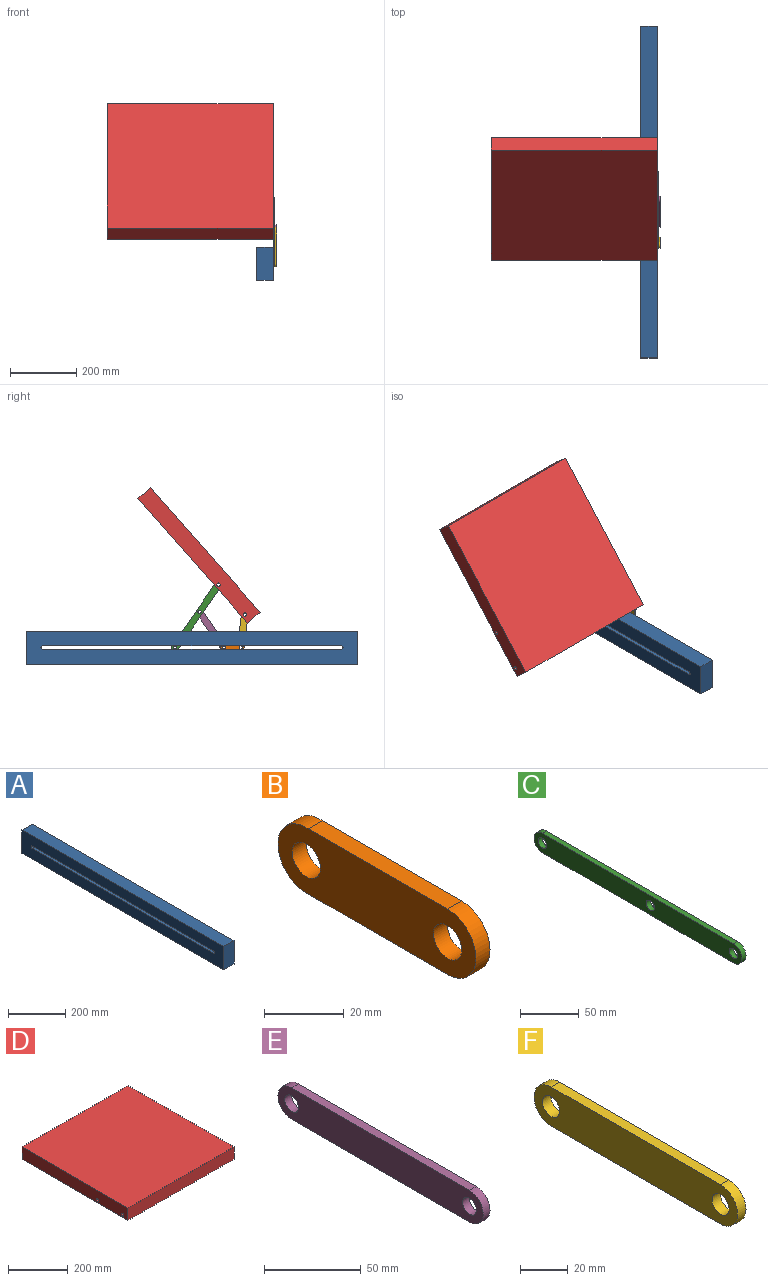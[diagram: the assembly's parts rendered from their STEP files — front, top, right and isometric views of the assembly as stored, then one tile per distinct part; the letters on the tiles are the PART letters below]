
ASSEMBLY  parts=6 mates=8
PART A: 10 faces, bbox 50x1000x100 mm
  f0: plane 1000x50mm, normal (0,0,1), area 50000mm2, adj f1,f7,f8,f9
  f1: plane 100x50mm, normal (0,-1,0), area 5000mm2, adj f0,f2,f8,f9
  f2: plane 1000x50mm, normal (0,0,-1), area 50000mm2, adj f1,f7,f8,f9
  f3: cylinder r=5mm len=50mm, axis (-1,0,0), area 785.4mm2, adj f4,f6,f8,f9
  f4: plane 900x50mm, normal (0,0,-1), area 45000mm2, adj f3,f5,f8,f9
  f5: cylinder r=5mm len=50mm, axis (-1,0,0), area 785.4mm2, adj f4,f6,f8,f9
  f6: plane 900x50mm, normal (0,0,1), area 45000mm2, adj f3,f5,f8,f9
  f7: plane 100x50mm, normal (0,1,0), area 5000mm2, adj f0,f2,f8,f9
  f8: plane 1000x100mm, normal (1,0,0), area 90921.5mm2, adj f0,f1,f2,f3,f4,f5,f6,f7
  f9: plane 1000x100mm, normal (-1,0,0), area 90921.5mm2, adj f0,f1,f2,f3,f4,f5,f6,f7
PART B: 8 faces, bbox 5x70x20 mm
  f0: cylinder r=10mm len=20mm, axis (-1,0,0), area 163.3mm2, adj f1,f4,f6,f7
  f1: plane 49.21x5mm, normal (0,0,1), area 246.1mm2, adj f0,f2,f6,f7
  f2: cylinder r=10mm len=20mm, axis (-1,0,0), area 157.7mm2, adj f1,f4,f6,f7
  f3: cylinder r=5mm len=10mm, axis (-1,0,0), area 157.1mm2, adj f6,f7
  f4: plane 49.41x5mm, normal (0,0,-1), area 247mm2, adj f0,f2,f6,f7
  f5: cylinder r=5mm len=10mm, axis (-1,0,0), area 157.1mm2, adj f6,f7
  f6: plane 70x20mm, normal (1,0,0), area 1156.1mm2, adj f0,f1,f2,f3,f4,f5
  f7: plane 70x20mm, normal (-1,0,0), area 1156.1mm2, adj f0,f1,f2,f3,f4,f5
PART C: 11 faces, bbox 5x250x20 mm
  f0: cylinder r=10mm len=5mm, axis (-1,0,0), area 2.8mm2, adj f1,f7,f9,f10
  f1: plane 128.96x5mm, normal (0,0,-1), area 644.8mm2, adj f0,f2,f9,f10
  f2: cylinder r=10mm len=20mm, axis (-1,0,0), area 160.9mm2, adj f1,f3,f9,f10
  f3: plane 230x5mm, normal (0,0,1), area 1150mm2, adj f2,f4,f9,f10
  f4: cylinder r=10mm len=20mm, axis (-1,0,0), area 157.1mm2, adj f3,f7,f9,f10
  f5: cylinder r=5mm len=10mm, axis (-1,0,0), area 157.1mm2, adj f9,f10
  f6: cylinder r=5mm len=10mm, axis (-1,0,0), area 157.1mm2, adj f9,f10
  f7: plane 99.72x5mm, normal (0,0,-1), area 498.6mm2, adj f0,f4,f9,f10
  f8: cylinder r=5mm len=10mm, axis (-1,0,0), area 157.1mm2, adj f9,f10
  f9: plane 250x20mm, normal (1,0,0), area 4676.2mm2, adj f0,f1,f2,f3,f4,f5,f6,f7
  f10: plane 250x20mm, normal (-1,0,0), area 4676.2mm2, adj f0,f1,f2,f3,f4,f5,f6,f7
PART D: 8 faces, bbox 500x500x50 mm
  f0: plane 500x500mm, normal (0,0,1), area 250000mm2, adj f1,f5,f6,f7
  f1: plane 500x50mm, normal (0,-1,0), area 25000mm2, adj f0,f2,f6,f7
  f2: plane 500x500mm, normal (0,0,-1), area 250000mm2, adj f1,f5,f6,f7
  f3: cylinder r=5mm len=500mm, axis (-1,0,0), area 15708mm2, adj f6,f7
  f4: cylinder r=5mm len=500mm, axis (-1,0,0), area 15708mm2, adj f6,f7
  f5: plane 500x50mm, normal (0,1,0), area 25000mm2, adj f0,f2,f6,f7
  f6: plane 500x50mm, normal (1,0,0), area 24842.9mm2, adj f0,f1,f2,f3,f4,f5
  f7: plane 500x50mm, normal (-1,0,0), area 24842.9mm2, adj f0,f1,f2,f3,f4,f5
PART E: 8 faces, bbox 5x150x20 mm
  f0: cylinder r=10mm len=20mm, axis (-1,0,0), area 157.6mm2, adj f1,f4,f6,f7
  f1: plane 129.68x5mm, normal (0,0,-1), area 648.4mm2, adj f0,f2,f6,f7
  f2: cylinder r=10mm len=20mm, axis (-1,0,0), area 158.7mm2, adj f1,f4,f6,f7
  f3: cylinder r=5mm len=10mm, axis (-1,0,0), area 157.1mm2, adj f6,f7
  f4: plane 129.9x5mm, normal (0,0,1), area 649.5mm2, adj f0,f2,f6,f7
  f5: cylinder r=5mm len=10mm, axis (-1,0,0), area 157.1mm2, adj f6,f7
  f6: plane 150x20mm, normal (1,0,0), area 2756.7mm2, adj f0,f1,f2,f3,f4,f5
  f7: plane 150x20mm, normal (-1,0,0), area 2756.7mm2, adj f0,f1,f2,f3,f4,f5
PART F: 8 faces, bbox 5x120x20 mm
  f0: cylinder r=10mm len=20mm, axis (-1,0,0), area 157.4mm2, adj f1,f4,f6,f7
  f1: plane 99.92x5mm, normal (0,0,-1), area 499.6mm2, adj f0,f2,f6,f7
  f2: cylinder r=10mm len=20mm, axis (-1,0,0), area 157.5mm2, adj f1,f4,f6,f7
  f3: cylinder r=5mm len=10mm, axis (-1,0,0), area 157.1mm2, adj f6,f7
  f4: plane 99.93x5mm, normal (0,0,1), area 499.6mm2, adj f0,f2,f6,f7
  f5: cylinder r=5mm len=10mm, axis (-1,0,0), area 157.1mm2, adj f6,f7
  f6: plane 120x20mm, normal (1,0,0), area 2157mm2, adj f0,f1,f2,f3,f4,f5
  f7: plane 120x20mm, normal (-1,0,0), area 2157mm2, adj f0,f1,f2,f3,f4,f5
PLACE A t=(111.49,-247.34,-467.57)mm fixed
PLACE B t=(161.49,-328.33,-485.69)mm
PLACE C rot(axis=(-1,0,0),55.4deg) t=(161.49,-236.68,-448.84)mm
PLACE D rot(axis=(1,0,0),48.6deg) t=(-338.51,-262.82,-192.33)mm
PLACE E rot(axis=(1,0,0),55.4deg) t=(166.49,-271.65,-428.98)mm
PLACE F rot(axis=(1,0,0),97.1deg) t=(166.49,-376.89,-415.76)mm
MATE revolute C.f0 <-> E.f2  axis (1,0,0) through (166.49,-267.83,-360.6)mm
MATE revolute D.f3 <-> F.f2  axis (1,0,0) through (161.49,-404.03,-368.33)mm
MATE pin_slot C.f2 <-> A.f3  axis (-1,0,0) through (161.49,-193.94,-467.57)mm
MATE revolute E.f0 <-> B.f0  axis (-1,0,0) through (166.49,-341.71,-467.57)mm
MATE revolute D.f4 <-> C.f4  axis (1,0,0) through (161.49,-324.66,-278.32)mm
MATE pin_slot B.f2 <-> A.f3  axis (-1,0,0) through (161.49,-391.71,-467.57)mm
MATE pin_slot B.f0 <-> A.f3  axis (-1,0,0) through (161.49,-341.71,-467.57)mm
MATE revolute F.f0 <-> B.f2  axis (-1,0,0) through (166.49,-391.71,-467.57)mm
